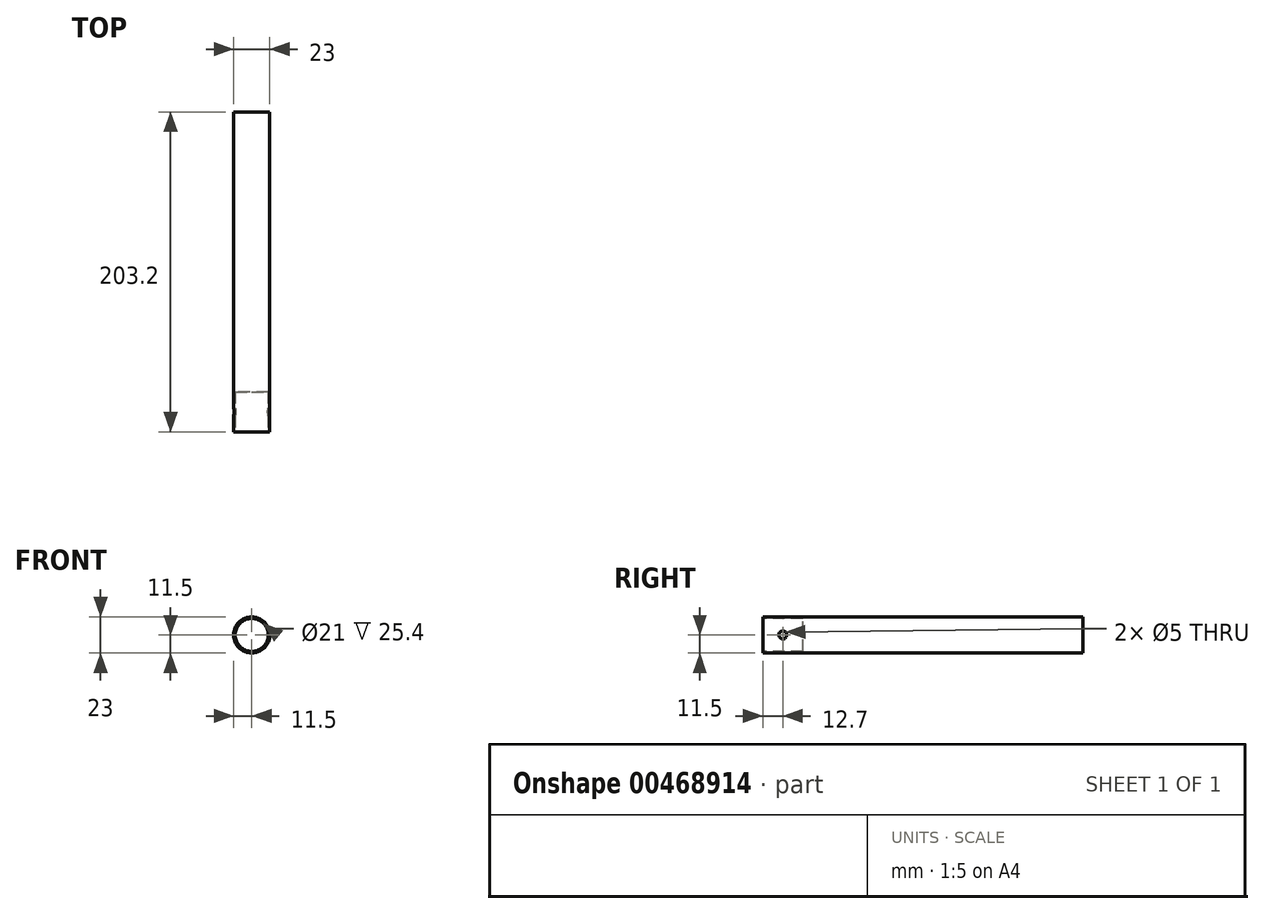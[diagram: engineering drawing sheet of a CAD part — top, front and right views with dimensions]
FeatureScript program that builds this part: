
annotation { "Feature Type Name" : "Feature", "Feature Type Description" : "" }
export const myFeature = defineFeature(function(context is Context, id is Id, definition is map)
    precondition{}
    {
        {
            var Q0;
            Q0=qCreatedBy(makeId("Front.planeOp"),FACE);
            var sketch = newSketch(context, id + "F0", { "sketchPlane" : qUnion([Q0])});
            skCircle(sketch, "E0", {"center": v(0, 0) * mm, "radius": 11.5 * mm});
            skCircle(sketch, "E1", {"center": v(0, 0) * mm, "radius": 10.5 * mm});
            skSolve(sketch);
        }
        {
            var Q0;
            Q0=makeQuery(id+"F0.imprint","IMPRINT",FACE,{"disambiguationData":[TD([[makeQuery(id+"F0.imprint","IMPRINT",EDGE,{"derivedFrom":sQuery(id+"F0.wireOp",EDGE,"E1")}),1.0]])]});
            var Q1;
            Q1=makeQuery(id+"F0.imprint","IMPRINT",FACE,{"disambiguationData":[TD([[makeQuery(id+"F0.imprint","IMPRINT",EDGE,{"derivedFrom":sQuery(id+"F0.wireOp",EDGE,"E0")}),1.0]])]});
            extrude(context, id + "F1", {"entities" : qUnion([Q0, Q1]), "oppositeDirection" : true, "depth" : 203.2 * mm});
        }
        {
            var Q0;
            Q0=makeQuery(id+"F0.imprint","IMPRINT",FACE,{"disambiguationData":[TD([[makeQuery(id+"F0.imprint","IMPRINT",EDGE,{"derivedFrom":sQuery(id+"F0.wireOp",EDGE,"E1")}),1.0]])]});
            extrude(context, id + "F2", {"entities" : qUnion([Q0]), "operationType" : NewBodyOperationType.REMOVE, "oppositeDirection" : true, "depth" : 25.4 * mm});
        }
        {
            var Q0;
            Q0=qCreatedBy(makeId("Right.planeOp"),FACE);
            var sketch = newSketch(context, id + "F3", { "sketchPlane" : qUnion([Q0])});
            skCircle(sketch, "E2", {"center": v(12.7, 0) * mm, "radius": 2.5 * mm});
            skSolve(sketch);
        }
        {
            var Q0;
            Q0 = qSketchRegion(id + "F3", true);
            extrude(context, id + "F4", {"entities" : qUnion([Q0]), "operationType" : NewBodyOperationType.REMOVE, "endBound" : BoundingType.SYMMETRIC, "oppositeDirection" : true, "depth" : 25.4 * mm});
        }
    });
